# Revit family: Окно двустворчатое VEKA  со сплошной фрамугой снизу и сверху
name_source: partatom
category: Окна
revit_build: Autodesk Revit 2016 (Build: 20150714_1515(x64)
units: mm (PartAtom-declared; Revit-internal decimal feet)

## family parameters
Всегда вертикально = Да
Заголовок OmniClass = Fixed Windows
Номер OmniClass = 23.30.20.17.11
Общий = Нет
Основа = Стена
При загрузке вырезать с полостями = Нет
Точка расчета площади = Нет

## types (5) — shared parameters
Аналитическая конструкция = <Нет>
Высота подоконника по умолчанию = 795 мм
Замыкание стены = По основе
Наименование = ОП ОСП 15-13 П
Обозначение = ГОСТ 23166-99
Описание = Окно
Отлив = <По категории>
Рама.Ширина = 80 мм
zero-valued in all types: Примерная высота, Примерная ширина

## per-type parameters (varying)
| type | VEKA_Цвет профиля | VEKA_Ширина профиля | Подоконник | Рама | Рама.Толщина | Стекло |
| SOFTLINE 70 | белый | 118 мм | <По категории> | <По категории> | 70 мм | <По категории> |
| EUROLINE 58 |  | 113 мм | <По категории> | <По категории> | 58 мм | <По категории> |
| SOFTLINE 82 |  | 124 мм | <По категории> | <По категории> | 82 мм | <По категории> |
| WHS 60 |  | 106 мм | <По категории> | <По категории> | 60 мм | <По категории> |
| WHS 72 |  | 111 мм | VEKA_Окна_ПВХ<БелыйМатовый | VEKA_Окна_ПВХ<БелыйМатовый | 72 мм | АС_Стекло |

## geometry (parser evidence)
native form markers: Blend x10, Sweep x4
no freeform markers — native parametric forms only
